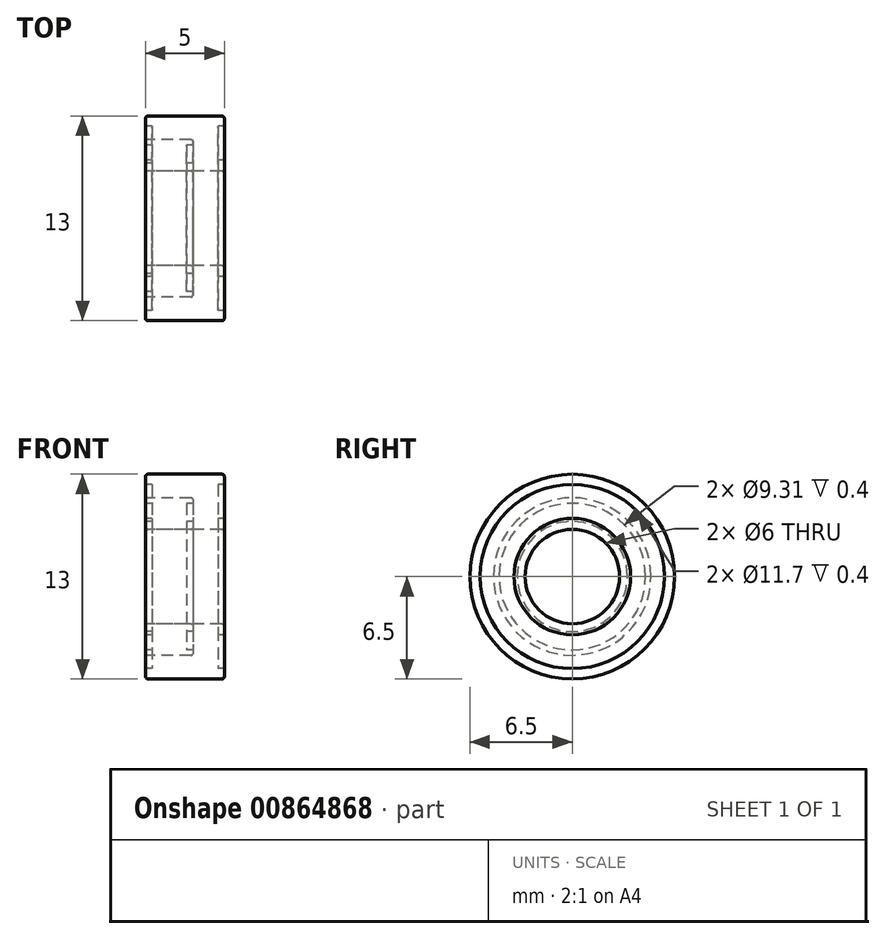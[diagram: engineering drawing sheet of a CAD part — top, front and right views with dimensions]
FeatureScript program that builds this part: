
annotation { "Feature Type Name" : "Feature", "Feature Type Description" : "" }
export const myFeature = defineFeature(function(context is Context, id is Id, definition is map)
    precondition{}
    {
        {
            var Q0;
            Q0=qCreatedBy(makeId("Front.planeOp"),FACE);
            var sketch = newSketch(context, id + "F0", { "sketchPlane" : qUnion([Q0])});
            skLineSegment(sketch, "E0", {"start": v(0.15, 6.5) * mm, "end": v(4.85, 6.5) * mm});
            skLineSegment(sketch, "E1", {"start": v(5, 6.35) * mm, "end": v(5, 5.85) * mm});
            skLineSegment(sketch, "E2", {"start": v(5, 5.85) * mm, "end": v(4.6, 5.85) * mm});
            skLineSegment(sketch, "E3", {"start": v(4.6, 5.85) * mm, "end": v(4.6, 3.7) * mm});
            skLineSegment(sketch, "E4", {"start": v(4.6, 3.7) * mm, "end": v(5, 3.7) * mm});
            skLineSegment(sketch, "E5", {"start": v(5, 3.7) * mm, "end": v(5, 3.15) * mm});
            skLineSegment(sketch, "E6", {"start": v(4.85, 3) * mm, "end": v(0.15, 3) * mm});
            skLineSegment(sketch, "E7", {"start": v(2.5, 6.5) * mm, "end": v(2.5, 3) * mm, "construction": true});
            skLineSegment(sketch, "E8.MirrorCS", {"start": v(0.4, 3.7) * mm, "end": v(0, 3.7) * mm});
            skLineSegment(sketch, "E9.MirrorCS", {"start": v(0, 5.85) * mm, "end": v(0.4, 5.85) * mm});
            skLineSegment(sketch, "E10.MirrorCS", {"start": v(0.4, 5.85) * mm, "end": v(0.4, 3.7) * mm});
            skLineSegment(sketch, "E11.MirrorCS", {"start": v(0, 3.7) * mm, "end": v(0, 3.15) * mm});
            skLineSegment(sketch, "E12.MirrorCS", {"start": v(0, 6.35) * mm, "end": v(0, 5.85) * mm});
            skLineSegment(sketch, "E13", {"start": v(0, 0) * mm, "end": v(6.84, 0) * mm, "construction": true});
            skPoint(sketch, "E14.visualSharp", {"position": v(0, 6.5) * mm});
            skArc(sketch, "E14.filletArc", {"start": v(0.15, 6.5) * mm, "mid": v(0.04, 6.46) * mm, "end": v(0, 6.35) * mm});
            skPoint(sketch, "E15.visualSharp", {"position": v(5, 6.5) * mm});
            skArc(sketch, "E15.filletArc", {"start": v(5, 6.35) * mm, "mid": v(4.96, 6.46) * mm, "end": v(4.85, 6.5) * mm});
            skPoint(sketch, "E16.visualSharp", {"position": v(0, 3) * mm});
            skArc(sketch, "E16.filletArc", {"start": v(0, 3.15) * mm, "mid": v(0.04, 3.04) * mm, "end": v(0.15, 3) * mm});
            skPoint(sketch, "E17.visualSharp", {"position": v(5, 3) * mm});
            skArc(sketch, "E17.filletArc", {"start": v(4.85, 3) * mm, "mid": v(4.96, 3.04) * mm, "end": v(5, 3.15) * mm});
            skSolve(sketch);
        }
        {
            var Q0;
            Q0=makeQuery(id+"F0.imprint","IMPRINT",FACE,{"disambiguationData":[TD([[makeQuery(id+"F0.imprint","IMPRINT",EDGE,{"derivedFrom":sQuery(id+"F0.wireOp",EDGE,"E0")}),-1.0]])]});
            var Q1;
            Q1=sQuery(id+"F0.wireOp",EDGE,"E13");
            revolve(context, id + "F1", {"surfaceOperationType" : NewSurfaceOperationType.NEW, "entities" : qUnion([Q0]), "axis" : qUnion([Q1]), "revolveType" : RevolveType.FULL});
        }
        {
            var Q0;
            Q0=qCreatedBy(makeId("Front.planeOp"),FACE);
            var sketch = newSketch(context, id + "F2", { "sketchPlane" : qUnion([Q0])});
            skLineSegment(sketch, "E18", {"start": v(0.1, 5) * mm, "end": v(2.9, 5) * mm});
            skLineSegment(sketch, "E19", {"start": v(3, 4.9) * mm, "end": v(3, 4.66) * mm});
            skLineSegment(sketch, "E20", {"start": v(3, 4.66) * mm, "end": v(2.6, 4.66) * mm});
            skLineSegment(sketch, "E21", {"start": v(2.6, 4.66) * mm, "end": v(2.6, 3.5) * mm});
            skLineSegment(sketch, "E22", {"start": v(2.6, 3.5) * mm, "end": v(3, 3.5) * mm});
            skLineSegment(sketch, "E23", {"start": v(3, 3.5) * mm, "end": v(3, 3.1) * mm});
            skLineSegment(sketch, "E24", {"start": v(2.9, 3) * mm, "end": v(0.1, 3) * mm});
            skLineSegment(sketch, "E25", {"start": v(1.5, 5) * mm, "end": v(1.5, 3) * mm, "construction": true});
            skLineSegment(sketch, "E26.MirrorCS", {"start": v(0.4, 3.5) * mm, "end": v(0, 3.5) * mm});
            skLineSegment(sketch, "E27.MirrorCS", {"start": v(0, 4.66) * mm, "end": v(0.4, 4.66) * mm});
            skLineSegment(sketch, "E28.MirrorCS", {"start": v(0.4, 4.66) * mm, "end": v(0.4, 3.5) * mm});
            skLineSegment(sketch, "E29.MirrorCS", {"start": v(0, 3.5) * mm, "end": v(0, 3.1) * mm});
            skLineSegment(sketch, "E30.MirrorCS", {"start": v(0, 4.9) * mm, "end": v(0, 4.66) * mm});
            skLineSegment(sketch, "E31", {"start": v(-132.32, 0) * mm, "end": v(0, 0) * mm, "construction": true});
            skPoint(sketch, "E32.visualSharp", {"position": v(0, 5) * mm});
            skArc(sketch, "E32.filletArc", {"start": v(0.1, 5) * mm, "mid": v(0.03, 4.97) * mm, "end": v(0, 4.9) * mm});
            skPoint(sketch, "E33.visualSharp", {"position": v(3, 5) * mm});
            skArc(sketch, "E33.filletArc", {"start": v(3, 4.9) * mm, "mid": v(2.97, 4.97) * mm, "end": v(2.9, 5) * mm});
            skPoint(sketch, "E34.visualSharp", {"position": v(0, 3) * mm});
            skArc(sketch, "E34.filletArc", {"start": v(0, 3.1) * mm, "mid": v(0.03, 3.03) * mm, "end": v(0.1, 3) * mm});
            skPoint(sketch, "E35.visualSharp", {"position": v(3, 3) * mm});
            skArc(sketch, "E35.filletArc", {"start": v(2.9, 3) * mm, "mid": v(2.97, 3.03) * mm, "end": v(3, 3.1) * mm});
            skLineSegment(sketch, "E36", {"start": v(0, 0) * mm, "end": v(0, 8.4) * mm, "construction": true});
            skSolve(sketch);
        }
        {
            var Q0;
            Q0 = qSketchRegion(id + "F2", true);
            var Q1;
            Q1=sQuery(id+"F2.wireOp",EDGE,"E31");
            revolve(context, id + "F3", {"surfaceOperationType" : NewSurfaceOperationType.NEW, "entities" : qUnion([Q0]), "axis" : qUnion([Q1]), "revolveType" : RevolveType.FULL});
        }
    });
